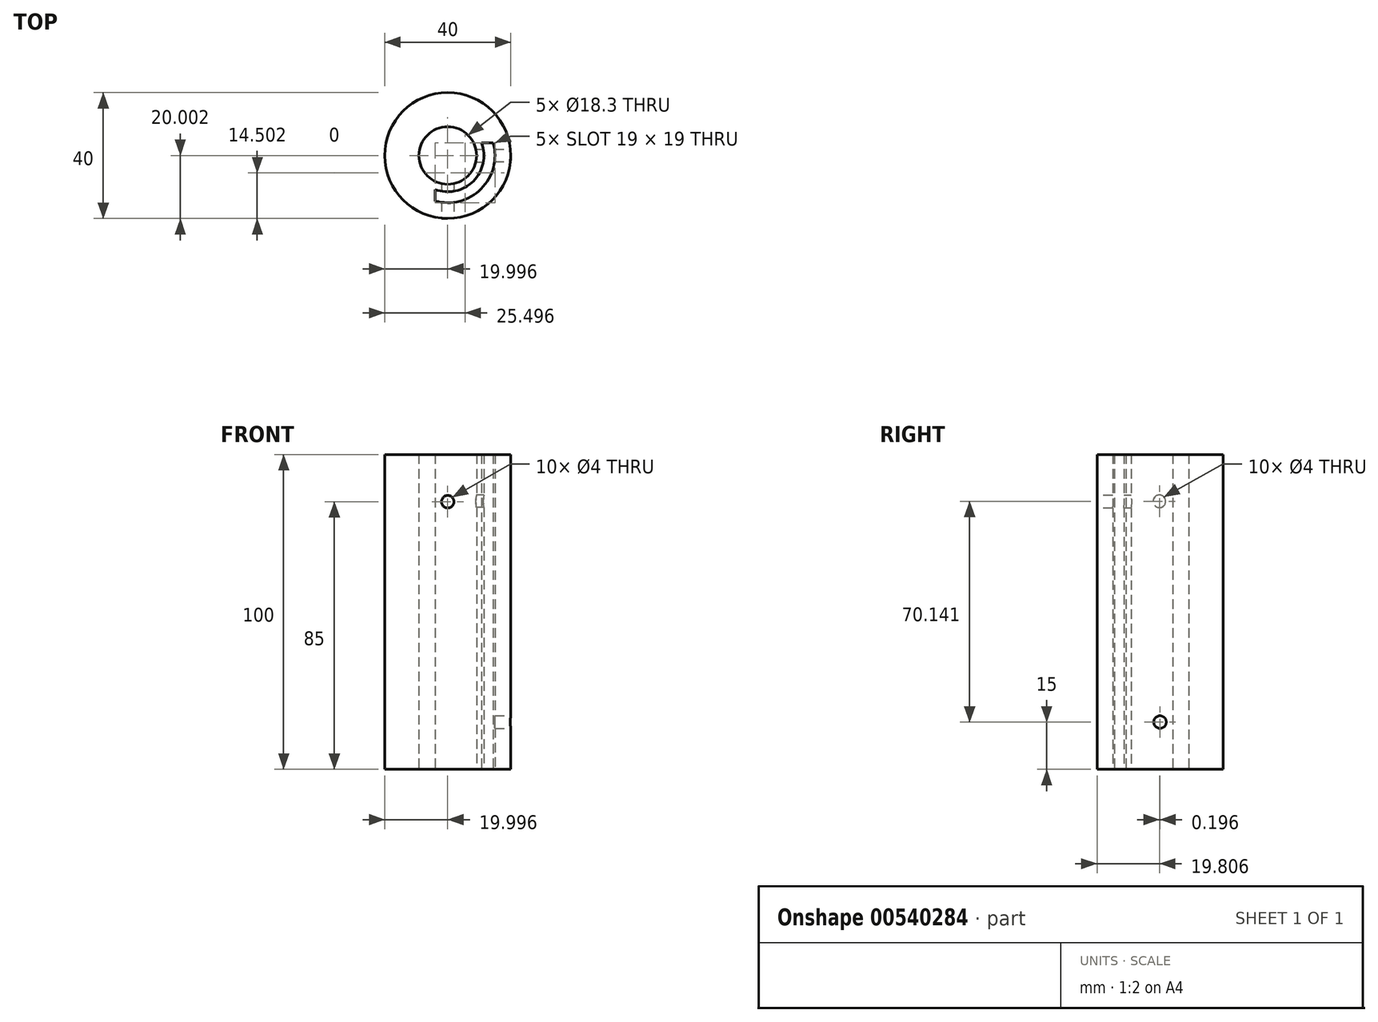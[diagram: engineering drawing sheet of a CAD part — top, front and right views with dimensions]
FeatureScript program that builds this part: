
annotation { "Feature Type Name" : "Feature", "Feature Type Description" : "" }
export const myFeature = defineFeature(function(context is Context, id is Id, definition is map)
    precondition{}
    {
        {
            var Q0;
            Q0=qCreatedBy(makeId("Top.planeOp"),FACE);
            var sketch = newSketch(context, id + "F0", { "sketchPlane" : qUnion([Q0])});
            skCircle(sketch, "E0", {"center": v(-32.11, 30.21) * mm, "radius": 9.15 * mm});
            skCircle(sketch, "E1", {"center": v(-32.11, 30.21) * mm, "radius": 20 * mm});
            skLineSegment(sketch, "E2.bottom", {"start": v(-12.11, 50.21) * mm, "end": v(-52.11, 50.21) * mm});
            skLineSegment(sketch, "E2.top", {"start": v(-12.11, 10.21) * mm, "end": v(-52.11, 10.21) * mm});
            skLineSegment(sketch, "E2.left", {"start": v(-12.11, 50.21) * mm, "end": v(-12.11, 10.21) * mm});
            skLineSegment(sketch, "E2.right", {"start": v(-52.11, 50.21) * mm, "end": v(-52.11, 10.21) * mm});
            skCircle(sketch, "E3", {"center": v(-32.11, 30.21) * mm, "radius": 11.5 * mm});
            skLineSegment(sketch, "E4.bottom", {"start": v(-32.11, 30.21) * mm, "end": v(-36.11, 30.21) * mm});
            skLineSegment(sketch, "E4.top", {"start": v(-32.11, 34.21) * mm, "end": v(-36.11, 34.21) * mm});
            skLineSegment(sketch, "E4.left", {"start": v(-32.11, 30.21) * mm, "end": v(-32.11, 34.21) * mm});
            skLineSegment(sketch, "E4.right", {"start": v(-36.11, 30.21) * mm, "end": v(-36.11, 34.21) * mm});
            skLineSegment(sketch, "E5", {"start": v(-36.11, 30.21) * mm, "end": v(-36.11, 10.62) * mm});
            skLineSegment(sketch, "E6", {"start": v(-32.11, 34.21) * mm, "end": v(-12.52, 34.21) * mm});
            skCircle(sketch, "E7", {"center": v(-32.11, 30.21) * mm, "radius": 15 * mm});
            skSolve(sketch);
        }
        {
            var Q0;
            Q0=makeQuery(id+"F0.imprint","IMPRINT",FACE,{"disambiguationData":[TD([[makeQuery(id+"F0.imprint","IMPRINT",EDGE,{"derivedFrom":sQuery(id+"F0.wireOp",EDGE,"E0")}),-1.0]])]});
            var Q1;
            {var subQ0=sQuery(id+"F0.wireOp",EDGE,"E2.bottom");var subQ1=sQuery(id+"F0.wireOp",EDGE,"E1");var subQ2=makeQuery(id+"F0.imprint","INTERSECT",VERTEX,{"derivedFrom":[subQ1,subQ0]});Q1=makeQuery(id+"F0.imprint","IMPRINT",FACE,{"disambiguationData":[TD([[makeQuery(id+"F0.imprint","IMPRINT",EDGE,{"disambiguationData":[TD([[subQ2,-1.0]])],"derivedFrom":subQ1}),-1.0]])]});}
            var Q2;
            {var subQ0=sQuery(id+"F0.wireOp",EDGE,"E2.bottom");var subQ1=sQuery(id+"F0.wireOp",EDGE,"E1");var subQ2=makeQuery(id+"F0.imprint","INTERSECT",VERTEX,{"derivedFrom":[subQ1,subQ0]});Q2=makeQuery(id+"F0.imprint","IMPRINT",FACE,{"disambiguationData":[TD([[makeQuery(id+"F0.imprint","IMPRINT",EDGE,{"disambiguationData":[TD([[subQ2,1.0]])],"derivedFrom":subQ1}),-1.0]])]});}
            var Q3;
            {var subQ0=sQuery(id+"F0.wireOp",EDGE,"E2.left");var subQ1=sQuery(id+"F0.wireOp",EDGE,"E1");var subQ2=makeQuery(id+"F0.imprint","INTERSECT",VERTEX,{"derivedFrom":[subQ1,subQ0]});Q3=makeQuery(id+"F0.imprint","IMPRINT",FACE,{"disambiguationData":[TD([[makeQuery(id+"F0.imprint","IMPRINT",EDGE,{"disambiguationData":[TD([[subQ2,1.0]])],"derivedFrom":subQ1}),-1.0]])]});}
            var Q4;
            {var subQ0=sQuery(id+"F0.wireOp",EDGE,"E2.right");var subQ1=sQuery(id+"F0.wireOp",EDGE,"E1");var subQ2=makeQuery(id+"F0.imprint","INTERSECT",VERTEX,{"derivedFrom":[subQ1,subQ0]});Q4=makeQuery(id+"F0.imprint","IMPRINT",FACE,{"disambiguationData":[TD([[makeQuery(id+"F0.imprint","IMPRINT",EDGE,{"disambiguationData":[TD([[subQ2,-1.0]])],"derivedFrom":subQ1}),-1.0]])]});}
            var Q5;
            {var subQ1=sQuery(id+"F0.wireOp",EDGE,"E1");var subQ5=sQuery(id+"F0.wireOp",EDGE,"E6");var subQ6=makeQuery(id+"F0.imprint","INTERSECT",VERTEX,{"derivedFrom":[subQ1,subQ5]});Q5=makeQuery(id+"F0.imprint","IMPRINT",FACE,{"disambiguationData":[TD([[makeQuery(id+"F0.imprint","IMPRINT",EDGE,{"disambiguationData":[TD([[subQ6,-1.0]])],"derivedFrom":subQ1}),1.0]])]});}
            var Q6;
            {var subQ1=sQuery(id+"F0.wireOp",EDGE,"E1");var subQ7=sQuery(id+"F0.wireOp",EDGE,"E6");var subQ8=makeQuery(id+"F0.imprint","INTERSECT",VERTEX,{"derivedFrom":[subQ1,subQ7]});Q6=makeQuery(id+"F0.imprint","IMPRINT",FACE,{"disambiguationData":[TD([[makeQuery(id+"F0.imprint","IMPRINT",EDGE,{"disambiguationData":[TD([[subQ8,1.0]])],"derivedFrom":subQ1}),1.0]])]});}
            var Q7;
            {var subQ0=sQuery(id+"F0.wireOp",EDGE,"E5");var subQ1=sQuery(id+"F0.wireOp",EDGE,"E3");var subQ2=makeQuery(id+"F0.imprint","INTERSECT",VERTEX,{"derivedFrom":[subQ1,subQ0]});Q7=makeQuery(id+"F0.imprint","IMPRINT",FACE,{"disambiguationData":[TD([[makeQuery(id+"F0.imprint","IMPRINT",EDGE,{"disambiguationData":[TD([[subQ2,1.0]])],"derivedFrom":subQ1}),-1.0]])]});}
            extrude(context, id + "F1", {"entities" : qUnion([Q0, Q1, Q2, Q3, Q4, Q5, Q6, Q7]), "depth" : 100 * mm, "offsetDistance" : 25 * mm});
        }
        {
            var Q0;
            Q0=makeQuery(id+"F1.opExtrude","SWEPT_FACE",FACE,{"disambiguationData":[OSD([sQuery(id+"F0.wireOp",EDGE,"E2.top")])]});
            var sketch = newSketch(context, id + "F2", { "sketchPlane" : qUnion([Q0])});
            skLineSegment(sketch, "E8", {"start": v(-52.11, 100) * mm, "end": v(-52.11, 70) * mm});
            skCircle(sketch, "E9", {"center": v(-32.11, 85) * mm, "radius": 2 * mm});
            skPoint(sketch, "E9.centerSnap0", {"position": v(-32.11, 100) * mm});
            skPoint(sketch, "E9.centerSnap1", {"position": v(-52.11, 85) * mm});
            skSolve(sketch);
        }
        {
            var Q0;
            Q0=makeQuery(id+"F2.imprint","IMPRINT",FACE,{"disambiguationData":[TD([[makeQuery(id+"F2.imprint","IMPRINT",EDGE,{"derivedFrom":sQuery(id+"F2.wireOp",EDGE,"E9")}),1.0]])]});
            extrude(context, id + "F3", {"entities" : qUnion([Q0]), "operationType" : NewBodyOperationType.REMOVE, "oppositeDirection" : true, "depth" : 15 * mm, "offsetDistance" : 25 * mm});
        }
        {
            var Q0;
            Q0=makeQuery(id+"F1.opExtrude","SWEPT_FACE",FACE,{"disambiguationData":[OSD([sQuery(id+"F0.wireOp",EDGE,"E2.left")])]});
            var sketch = newSketch(context, id + "F4", { "sketchPlane" : qUnion([Q0])});
            skLineSegment(sketch, "E10", {"start": v(10.21, 0) * mm, "end": v(10.21, 30) * mm});
            skCircle(sketch, "E11", {"center": v(30.21, 15) * mm, "radius": 2 * mm});
            skPoint(sketch, "E11.centerSnap0", {"position": v(10.21, 15) * mm});
            skPoint(sketch, "E11.centerSnap1", {"position": v(30.21, 0) * mm});
            skLineSegment(sketch, "E12", {"start": v(10.21, 100) * mm, "end": v(10.21, 70) * mm});
            skCircle(sketch, "E13", {"center": v(30.21, 85) * mm, "radius": 2 * mm});
            skPoint(sketch, "E13.centerSnap0", {"position": v(30.21, 100) * mm});
            skPoint(sketch, "E13.centerSnap1", {"position": v(10.21, 85) * mm});
            skSolve(sketch);
        }
        {
            var Q0;
            Q0=makeQuery(id+"F4.imprint","IMPRINT",FACE,{"disambiguationData":[TD([[makeQuery(id+"F4.imprint","IMPRINT",EDGE,{"derivedFrom":sQuery(id+"F4.wireOp",EDGE,"E11")}),1.0]])]});
            extrude(context, id + "F5", {"entities" : qUnion([Q0]), "operationType" : NewBodyOperationType.REMOVE, "oppositeDirection" : true, "depth" : 6 * mm, "offsetDistance" : 25 * mm});
        }
        {
            var Q0;
            {var subQ0=sQuery(id+"F0.wireOp",EDGE,"E2.left");var subQ1=sQuery(id+"F0.wireOp",EDGE,"E1");var subQ2=makeQuery(id+"F0.imprint","INTERSECT",VERTEX,{"derivedFrom":[subQ1,subQ0]});Q0=makeQuery(id+"F0.imprint","IMPRINT",FACE,{"disambiguationData":[TD([[makeQuery(id+"F0.imprint","IMPRINT",EDGE,{"disambiguationData":[TD([[subQ2,1.0]])],"derivedFrom":subQ1}),-1.0]])]});}
            var Q1;
            {var subQ0=sQuery(id+"F0.wireOp",EDGE,"E2.right");var subQ1=sQuery(id+"F0.wireOp",EDGE,"E1");var subQ2=makeQuery(id+"F0.imprint","INTERSECT",VERTEX,{"derivedFrom":[subQ1,subQ0]});Q1=makeQuery(id+"F0.imprint","IMPRINT",FACE,{"disambiguationData":[TD([[makeQuery(id+"F0.imprint","IMPRINT",EDGE,{"disambiguationData":[TD([[subQ2,-1.0]])],"derivedFrom":subQ1}),-1.0]])]});}
            var Q2;
            {var subQ0=sQuery(id+"F0.wireOp",EDGE,"E2.bottom");var subQ1=sQuery(id+"F0.wireOp",EDGE,"E1");var subQ2=makeQuery(id+"F0.imprint","INTERSECT",VERTEX,{"derivedFrom":[subQ1,subQ0]});Q2=makeQuery(id+"F0.imprint","IMPRINT",FACE,{"disambiguationData":[TD([[makeQuery(id+"F0.imprint","IMPRINT",EDGE,{"disambiguationData":[TD([[subQ2,-1.0]])],"derivedFrom":subQ1}),-1.0]])]});}
            var Q3;
            {var subQ0=sQuery(id+"F0.wireOp",EDGE,"E2.bottom");var subQ1=sQuery(id+"F0.wireOp",EDGE,"E1");var subQ2=makeQuery(id+"F0.imprint","INTERSECT",VERTEX,{"derivedFrom":[subQ1,subQ0]});Q3=makeQuery(id+"F0.imprint","IMPRINT",FACE,{"disambiguationData":[TD([[makeQuery(id+"F0.imprint","IMPRINT",EDGE,{"disambiguationData":[TD([[subQ2,1.0]])],"derivedFrom":subQ1}),-1.0]])]});}
            extrude(context, id + "F6", {"entities" : qUnion([Q0, Q1, Q2, Q3]), "operationType" : NewBodyOperationType.REMOVE, "endBound" : BoundingType.THROUGH_ALL, "depth" : 25 * mm, "offsetDistance" : 25 * mm});
        }
        {
            var Q0;
            Q0=qCreatedBy(makeId("Right.planeOp"),FACE);
            cPlane(context, id + "F7", {"entities" : qUnion([Q0]), "cplaneType" : CPlaneType.OFFSET, "offset" : 30 * mm, "oppositeDirection" : true, "width" : 150 * mm, "height" : 150 * mm});
        }
        {
            var Q0;
            Q0=qCreatedBy(id+"F7.planeOp",FACE);
            var sketch = newSketch(context, id + "F8", { "sketchPlane" : qUnion([Q0])});
            skCircle(sketch, "E14", {"center": v(30.02, 85.14) * mm, "radius": 2 * mm});
            skSolve(sketch);
        }
        {
            var Q0;
            Q0 = qSketchRegion(id + "F8", true);
            extrude(context, id + "F9", {"entities" : qUnion([Q0]), "operationType" : NewBodyOperationType.REMOVE, "depth" : 10 * mm, "offsetDistance" : 25 * mm});
        }
    });
